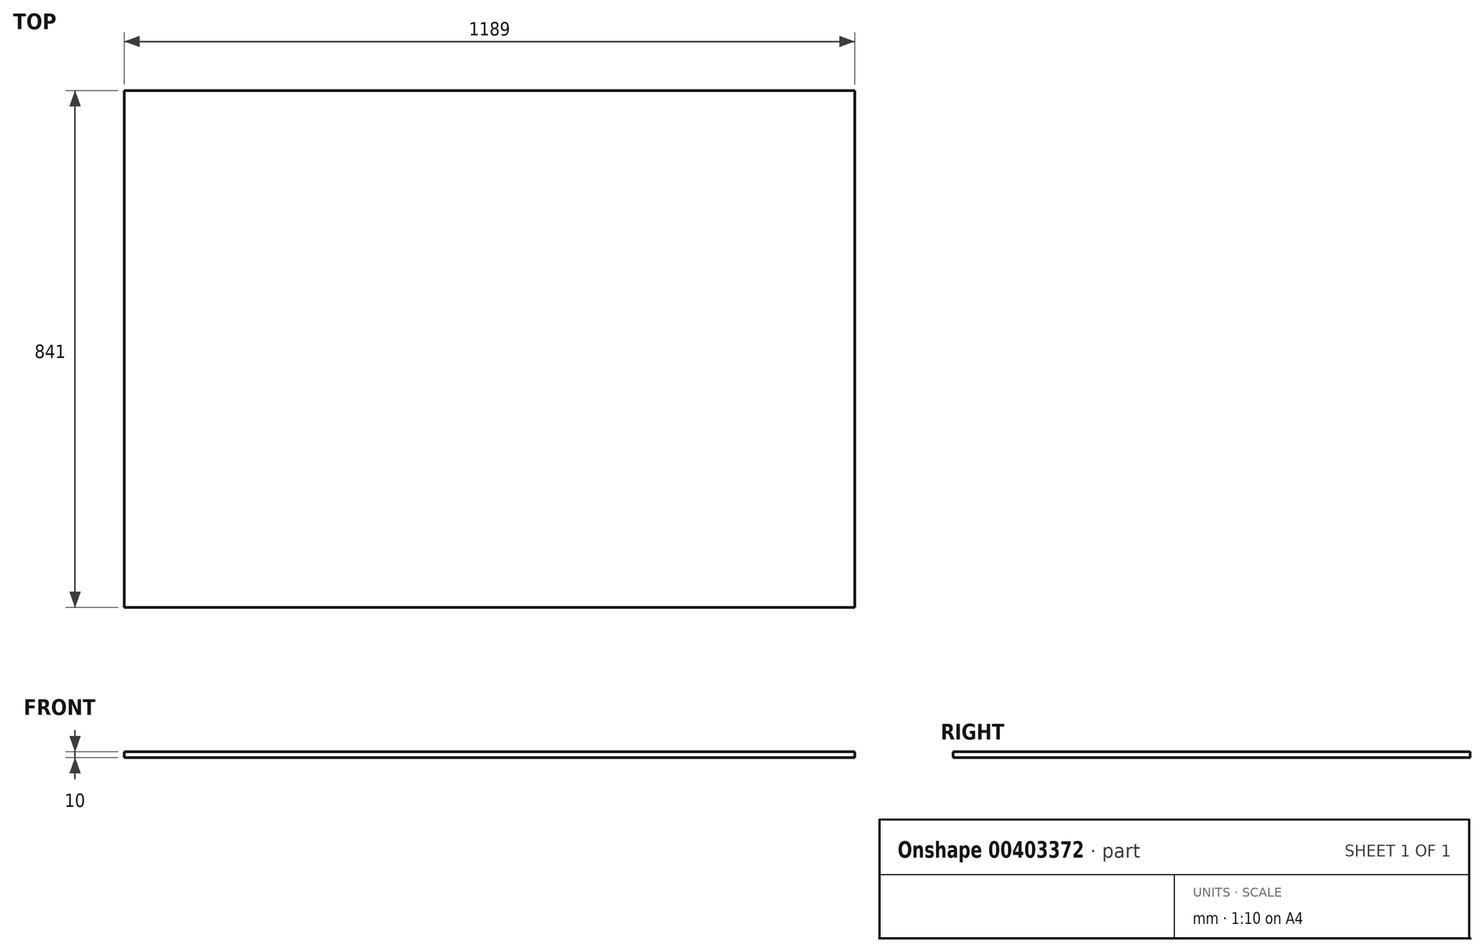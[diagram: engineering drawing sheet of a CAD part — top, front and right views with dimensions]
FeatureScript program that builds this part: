
annotation { "Feature Type Name" : "Feature", "Feature Type Description" : "" }
export const myFeature = defineFeature(function(context is Context, id is Id, definition is map)
    precondition{}
    {
        {
            assignVariable(context, id + "F0", {"name" : "T", "anyValue" : 10});
        }
        {
            var Q0;
            Q0=qCreatedBy(makeId("Top.planeOp"),FACE);
            var sketch = newSketch(context, id + "F1", { "sketchPlane" : qUnion([Q0])});
            skLineSegment(sketch, "E0.bottom", {"start": v(594.5, 420.5) * mm, "end": v(-594.5, 420.5) * mm});
            skLineSegment(sketch, "E0.top", {"start": v(594.5, -420.5) * mm, "end": v(-594.5, -420.5) * mm});
            skLineSegment(sketch, "E0.left", {"start": v(594.5, 420.5) * mm, "end": v(594.5, -420.5) * mm});
            skLineSegment(sketch, "E0.right", {"start": v(-594.5, 420.5) * mm, "end": v(-594.5, -420.5) * mm});
            skLineSegment(sketch, "E1", {"start": v(0, 420.5) * mm, "end": v(0, -420.5) * mm, "construction": true});
            skLineSegment(sketch, "E2", {"start": v(-594.5, 0) * mm, "end": v(594.5, 0) * mm, "construction": true});
            skSolve(sketch);
        }
        {
            var Q0;
            Q0=makeQuery(id+"F1.imprint","IMPRINT",FACE,{"disambiguationData":[TD([[makeQuery(id+"F1.imprint","IMPRINT",EDGE,{"derivedFrom":sQuery(id+"F1.wireOp",EDGE,"E0.bottom")}),1.0]])]});
            extrude(context, id + "F2", {"entities" : qUnion([Q0]), "endBound" : BoundingType.SYMMETRIC, "depth" : (getVariable(context, 'T')) * mm});
        }
    });
